AUTODESK INVENTOR PART (.ipt)
format: ipt  version: 2021.3 (Build 253353000, 353)  size: 122,880 bytes
history: native  units: mm
features: sketch x1
ambient origin geometry x8: Origin, YZ Plane, XZ Plane, XY Plane, X Axis, Y Axis, Z Axis, Center Point
feature tree (1):
  sketch  "Sketch1"  dims[d0=700.0mm d1=700.0mm d2=10.0mm d3=20.0mm d9=10.0mm d10=10.0mm d11=10.0mm d12=10.0mm d13=10.0mm d14=10.0mm d17=10.0mm d18=10.0mm d19=70.0mm d20=55.0mm d21=100.0mm]
